# Revit family: BC_Hitachi_Yutaki-M_LOD400
name_source: partatom
category: Equipement de génie climatique
revit_build: Autodesk Revit 2017 (Build: 20160225_1515(x64)
units: mm (PartAtom-declared; Revit-internal decimal feet)

## family parameters
Basée sur le plan de construction = Non
Cote de connecteur circulaire = Utiliser le diamètre
Couper avec des vides une fois chargée = Non
Numéro OmniClass = 23.75.70.17
Partagée = Non
Point de calcul de pièce = Non
Titre OmniClass = Water Heated and Cooled Terminal Heating and Cooling Units
Toujours verticalement = Oui
Type d'élément = Normal

## types (2) — shared parameters
Application = Heating, Cooling, DHW with external tank
BC_MODEL_ID = 151768
BC_OBJECT_ID = 29194
BC_OBJECT_VERSION = #5
Description = Yutaki M Monobloc System (R32)
Expansion vessel - internal water volume = 0.01 m³
Fabricant = Hitachi
Frequency = 50 Hz
Global Warming Potential (GWP) = 675
Heat Pump Type = Air-to-Water heat pump
Manufacturer = Hitachi Air Conditioning Europe SAS
MasterFormat = Split-System Air-Conditioners
Masterformat Code = 23 81 26
Material = White Metal
Minimum installation water volume = 0.03 m³
Modèle = Yutaki M R32
Nominal Voltage = 230 V
Number of Phases = 1
OMNICLASS Table 23 Code  = 23-33 39 11
Omniclass = Air Conditioners
Outlet water temperature (Cooling) = 5~22
Outlet water temperature (Heating) = 20~60
Overall Depth = 300 mm
Overall Height = 704 mm  [stored 2.30971 ft]
Overall Width = 1278 mm  [stored 4.19291 ft]
Refrigerant Type = R32
Service Space Material = Service Space
Standby power (PSB)  (Average climate) = 0 kW
Support Material = Support
Uniformat = Distribution Systems
Uniformat code = D3040
Working range (cooling) = 10~46
Working range (heating) = -20~25

## per-type parameters (varying)
| type | Annual energy consumption (QHE) 35°C application | Annual energy consumption (QHE) 55°C application | BC_VARIANT_ID | COP (A7/W35) | Commentaires du type | EER (A35/W18) | EER (A35/W7) | Maximum Current | Maximum cooling capacity (A35/W18) | Maximum cooling capacity (A35/W7) | Maximum heating capacity (A-7/W35) | Maximum heating capacity (A-7/W55) | Nominal Water Flow | Nominal cooling capacity (A35/W18) | Nominal cooling capacity (A35/W7) | Nominal energy efficiency 35°C (ηS) | Nominal energy efficiency 55°C (ηS) | Nominal heating capacity (A7/W35) | Refrigerant charge before shipment | SCOP 35°C (Average conditions) | SCOP 55°C (Average conditions) | SEER (+18°C / +23°C) | Sound power OU |
| RASM-2VRE | 1798 kWh | 2401 kWh | 190668 | 5.25 | Yutaki M 2HP (R32) | 5.4 | 4 | 11 A | 6.4 kW | 5 kW | 5.3 kW | 4.2 kW | 0.2 L/s | 5.5 kW | 4 kW | 181 | 133 | 4.3 kW | 1.20 kg | 4.6 | 3.4 | 8.04 | 61 |
| RASM-3VRE | 3068 kWh | 3724 kWh | 190669 | 4.6 | Yutaki M 3HP (R32) | 5 | 3.35 | 16 A | 9 kW | 7 kW | 7.5 kW | 5.5 kW | 0.4 L/s | 7 kW | 6.5 kW | 177 | 125 | 8 kW | 1.30 kg | 4.5 | 3.2 | 8.35 | 67 |

note: column(s) folded — value = type name in every type: Reference

note: [stored X ft] marks values corroborated as IEEE doubles in the binary element streams (Revit-internal decimal feet)
